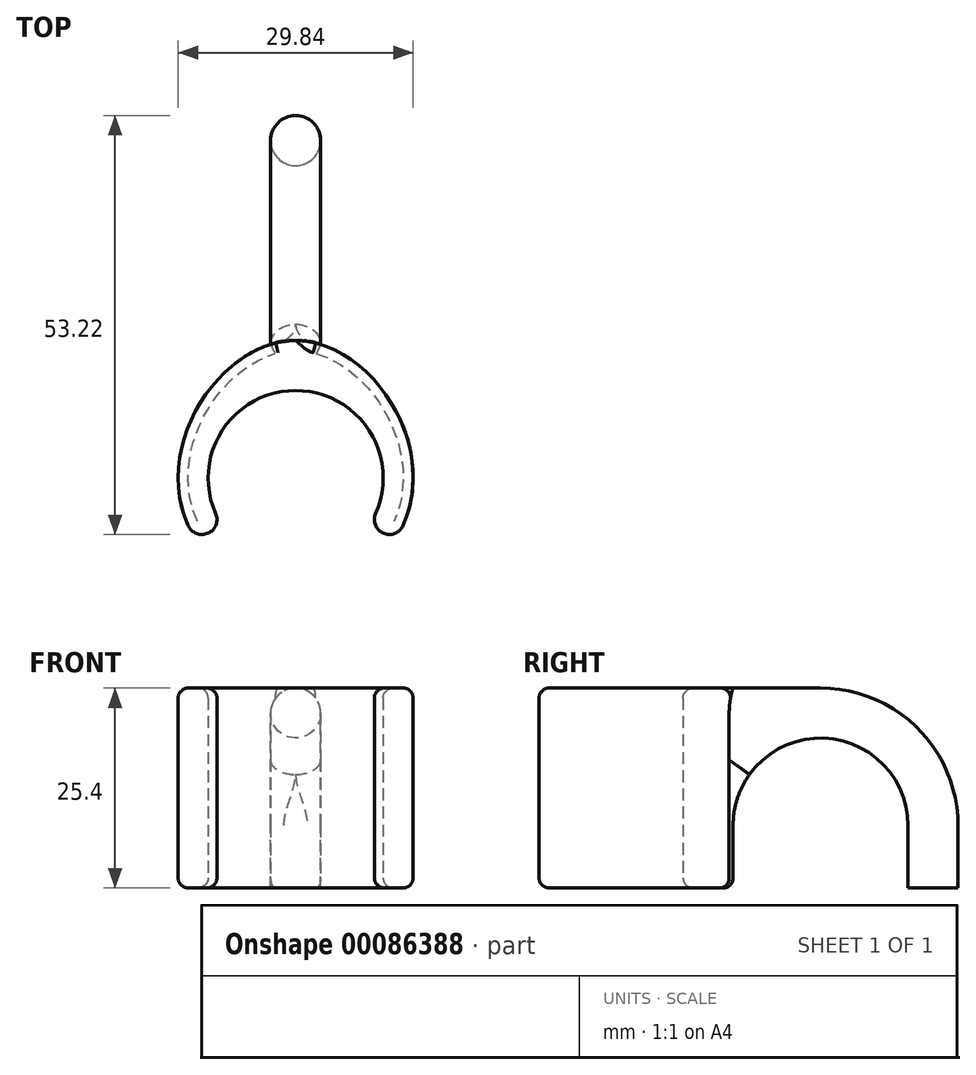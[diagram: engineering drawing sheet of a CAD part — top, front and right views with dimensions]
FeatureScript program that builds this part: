
annotation { "Feature Type Name" : "Feature", "Feature Type Description" : "" }
export const myFeature = defineFeature(function(context is Context, id is Id, definition is map)
    precondition{}
    {
        {
            var Q0;
            Q0=qCreatedBy(makeId("Top.planeOp"),FACE);
            var sketch = newSketch(context, id + "F0", { "sketchPlane" : qUnion([Q0])});
            skArc(sketch, "E0", {"start": v(-10.16, -4.5) * mm, "mid": v(0, -11.11) * mm, "end": v(10.16, -4.5) * mm, "construction": true});
            skArc(sketch, "E1", {"start": v(10.16, -4.5) * mm, "mid": v(0, 11.11) * mm, "end": v(-10.16, -4.5) * mm});
            skPoint(sketch, "E2.centerSnap0", {"position": v(0, 11.11) * mm});
            skLineSegment(sketch, "E3", {"start": v(-10.16, -4.5) * mm, "end": v(-13.64, -6.04) * mm, "construction": true});
            skLineSegment(sketch, "E4", {"start": v(10.16, -4.5) * mm, "end": v(13.64, -6.04) * mm, "construction": true});
            skFitSpline(sketch, "E5", {"points": [v(-13.64, -6.04) * mm, v(0, 17.46) * mm, v(13.64, -6.04) * mm], "startDerivative": vector(-28.3, 63.88) * mm, "endDerivative": vector(-28.3, -63.88) * mm});
            skLineSegment(sketch, "E6", {"start": v(11.11, 0) * mm, "end": v(14.92, 0) * mm, "construction": true});
            skArc(sketch, "E7", {"start": v(-13.64, -6.04) * mm, "mid": v(-11.13, -7.01) * mm, "end": v(-10.16, -4.5) * mm});
            skArc(sketch, "E8", {"start": v(10.16, -4.5) * mm, "mid": v(11.13, -7.01) * mm, "end": v(13.64, -6.04) * mm});
            skSolve(sketch);
        }
        {
            var Q0;
            Q0 = qSketchRegion(id + "F0", true);
            extrude(context, id + "F1", {"entities" : qUnion([Q0]), "depth" : 25.4 * mm});
        }
        {
            var Q0;
            Q0=qCreatedBy(makeId("Right.planeOp"),FACE);
            var sketch = newSketch(context, id + "F2", { "sketchPlane" : qUnion([Q0])});
            skLineSegment(sketch, "E9.top", {"start": v(11.11, 25.4) * mm, "end": v(28.57, 25.4) * mm});
            skLineSegment(sketch, "E9.left", {"start": v(11.11, 0) * mm, "end": v(11.11, 25.4) * mm});
            skLineSegment(sketch, "E9.right", {"start": v(46.04, 0) * mm, "end": v(46.04, 7.94) * mm});
            skLineSegment(sketch, "E10", {"start": v(11.11, 0) * mm, "end": v(17.46, 0) * mm});
            skLineSegment(sketch, "E11", {"start": v(17.46, 0) * mm, "end": v(17.46, 7.94) * mm});
            skArc(sketch, "E12", {"start": v(39.69, 7.94) * mm, "mid": v(28.58, 19.05) * mm, "end": v(17.46, 7.94) * mm});
            skLineSegment(sketch, "E13", {"start": v(39.69, 7.94) * mm, "end": v(39.69, 0) * mm});
            skLineSegment(sketch, "E14", {"start": v(39.69, 0) * mm, "end": v(46.04, 0) * mm});
            skArc(sketch, "E15", {"start": v(46.04, 7.94) * mm, "mid": v(40.92, 20.29) * mm, "end": v(28.57, 25.4) * mm});
            skSolve(sketch);
        }
        {
            var Q0;
            Q0 = qSketchRegion(id + "F2", true);
            extrude(context, id + "F3", {"entities" : qUnion([Q0]), "operationType" : NewBodyOperationType.ADD, "endBound" : BoundingType.SYMMETRIC, "depth" : 6.35 * mm});
        }
        {
            var Q0;
            Q0=makeQuery(id+"F3.opExtrude","CAP_EDGE",EDGE,{"disambiguationData":[OSD([sQuery(id+"F2.wireOp",EDGE,"E12")])],"isStart":true});
            var Q1;
            Q1=makeQuery(id+"F3.opExtrude","CAP_EDGE",EDGE,{"disambiguationData":[OSD([sQuery(id+"F2.wireOp",EDGE,"E12")])],"isStart":false});
            var Q2;
            Q2=makeQuery(id+"F3.opExtrude","CAP_EDGE",EDGE,{"disambiguationData":[OSD([sQuery(id+"F2.wireOp",EDGE,"E13")])],"isStart":false});
            var Q3;
            Q3=makeQuery(id+"F3.opExtrude","CAP_EDGE",EDGE,{"disambiguationData":[OSD([sQuery(id+"F2.wireOp",EDGE,"E11")])],"isStart":false});
            var Q4;
            Q4=makeQuery(id+"F3.opExtrude","CAP_EDGE",EDGE,{"disambiguationData":[OSD([sQuery(id+"F2.wireOp",EDGE,"E11")])],"isStart":true});
            var Q5;
            Q5=makeQuery(id+"F3.opExtrude","CAP_EDGE",EDGE,{"disambiguationData":[OSD([sQuery(id+"F2.wireOp",EDGE,"E13")])],"isStart":true});
            var Q6;
            Q6=makeQuery(id+"F3.opExtrude","CAP_EDGE",EDGE,{"disambiguationData":[OSD([sQuery(id+"F2.wireOp",EDGE,"E9.right")])],"isStart":false});
            var Q7;
            Q7=makeQuery(id+"F3.opExtrude","CAP_EDGE",EDGE,{"disambiguationData":[OSD([sQuery(id+"F2.wireOp",EDGE,"E15")])],"isStart":true});
            fillet(context, id + "F4", {"entities" : qUnion([Q0, Q1, Q2, Q3, Q4, Q5, Q6, Q7]), "radius" : 3.17 * mm, "tangentPropagation" : true, "allowEdgeOverflow" : false});
        }
        {
            var Q0;
            {var subQ1=sQuery(id+"F0.wireOp",EDGE,"E7");var subQ2=sQuery(id+"F0.wireOp",EDGE,"E5");Q0=makeQuery(id+"F3.boolean.opBoolean","SPLIT",EDGE,{"disambiguationData":[TD([makeQuery(id+"F1.opExtrude","SWEPT_FACE",FACE,{"disambiguationData":[OSD([subQ1])]})])],"derivedFrom":makeQuery(id+"F1.opExtrude","CAP_EDGE",EDGE,{"disambiguationData":[OSD([subQ2])],"isStart":false})});}
            var Q1;
            {var subQ1=sQuery(id+"F0.wireOp",EDGE,"E8");var subQ2=sQuery(id+"F0.wireOp",EDGE,"E5");Q1=makeQuery(id+"F3.boolean.opBoolean","SPLIT",EDGE,{"disambiguationData":[TD([makeQuery(id+"F1.opExtrude","SWEPT_FACE",FACE,{"disambiguationData":[OSD([subQ1])]})])],"derivedFrom":makeQuery(id+"F1.opExtrude","CAP_EDGE",EDGE,{"disambiguationData":[OSD([subQ2])],"isStart":false})});}
            var Q2;
            Q2=makeQuery(id+"F1.opExtrude","CAP_EDGE",EDGE,{"disambiguationData":[OSD([sQuery(id+"F0.wireOp",EDGE,"E1")])],"isStart":false});
            var Q3;
            Q3=makeQuery(id+"F1.opExtrude","CAP_EDGE",EDGE,{"disambiguationData":[OSD([sQuery(id+"F0.wireOp",EDGE,"E8")])],"isStart":false});
            var Q4;
            Q4=makeQuery(id+"F1.opExtrude","CAP_EDGE",EDGE,{"disambiguationData":[OSD([sQuery(id+"F0.wireOp",EDGE,"E7")])],"isStart":false});
            var Q5;
            {var subQ0=sQuery(id+"F0.wireOp",EDGE,"E8");var subQ1=sQuery(id+"F0.wireOp",EDGE,"E5");Q5=makeQuery(id+"F3.boolean.opBoolean","SPLIT",EDGE,{"disambiguationData":[TD([makeQuery(id+"F1.opExtrude","SWEPT_FACE",FACE,{"disambiguationData":[OSD([subQ0])]})])],"derivedFrom":makeQuery(id+"F1.opExtrude","CAP_EDGE",EDGE,{"disambiguationData":[OSD([subQ1])],"isStart":true})});}
            var Q6;
            Q6=makeQuery(id+"F3.opExtrude","SWEPT_EDGE",EDGE,{"disambiguationData":[OSD([sQuery(id+"F2.wireOp",EDGE,"E10"),sQuery(id+"F2.wireOp",EDGE,"E11")])]});
            var Q7;
            Q7=makeQuery(id+"F4.opFillet","BLEND_EDGE",EDGE,{"blendedFrom":[makeQuery(id+"F3.opExtrude","CAP_EDGE",EDGE,{"disambiguationData":[OSD([sQuery(id+"F2.wireOp",EDGE,"E13")])],"isStart":false}),makeQuery(id+"F3.opExtrude","SWEPT_FACE",FACE,{"disambiguationData":[OSD([sQuery(id+"F2.wireOp",EDGE,"E14")])]})],"blendedInto":[makeQuery(id+"F3.opExtrude","SWEPT_FACE",FACE,{"disambiguationData":[OSD([sQuery(id+"F2.wireOp",EDGE,"E14")])]})]});
            fillet(context, id + "F5", {"entities" : qUnion([Q0, Q1, Q2, Q3, Q4, Q5, Q6, Q7]), "radius" : 1.27 * mm, "tangentPropagation" : true, "allowEdgeOverflow" : false});
        }
    });
